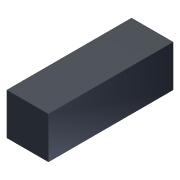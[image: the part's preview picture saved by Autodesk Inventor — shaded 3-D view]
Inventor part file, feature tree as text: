
AUTODESK INVENTOR PART (.ipt)
format: ipt  version: 2012 (Build 160160000, 160)  size: 70,144 bytes
history: native  units: in
note: dims shown in document units (in); Inventor stores cm internally (conversion verified against a paired STEP export)
features: extrude x1, sketch x1
ambient origin geometry x8: Origin, YZ Plane, XZ Plane, XY Plane, X Axis, Y Axis, Z Axis, Center Point
bodies: Solid1 (feature_tree)
feature tree (2):
  extrude  "Extrusion1"  Depth=4.0in
  sketch  "Sketch1"  dims[d0=4.0in d1=4.0in d2=12.0in d3=0.0in]
